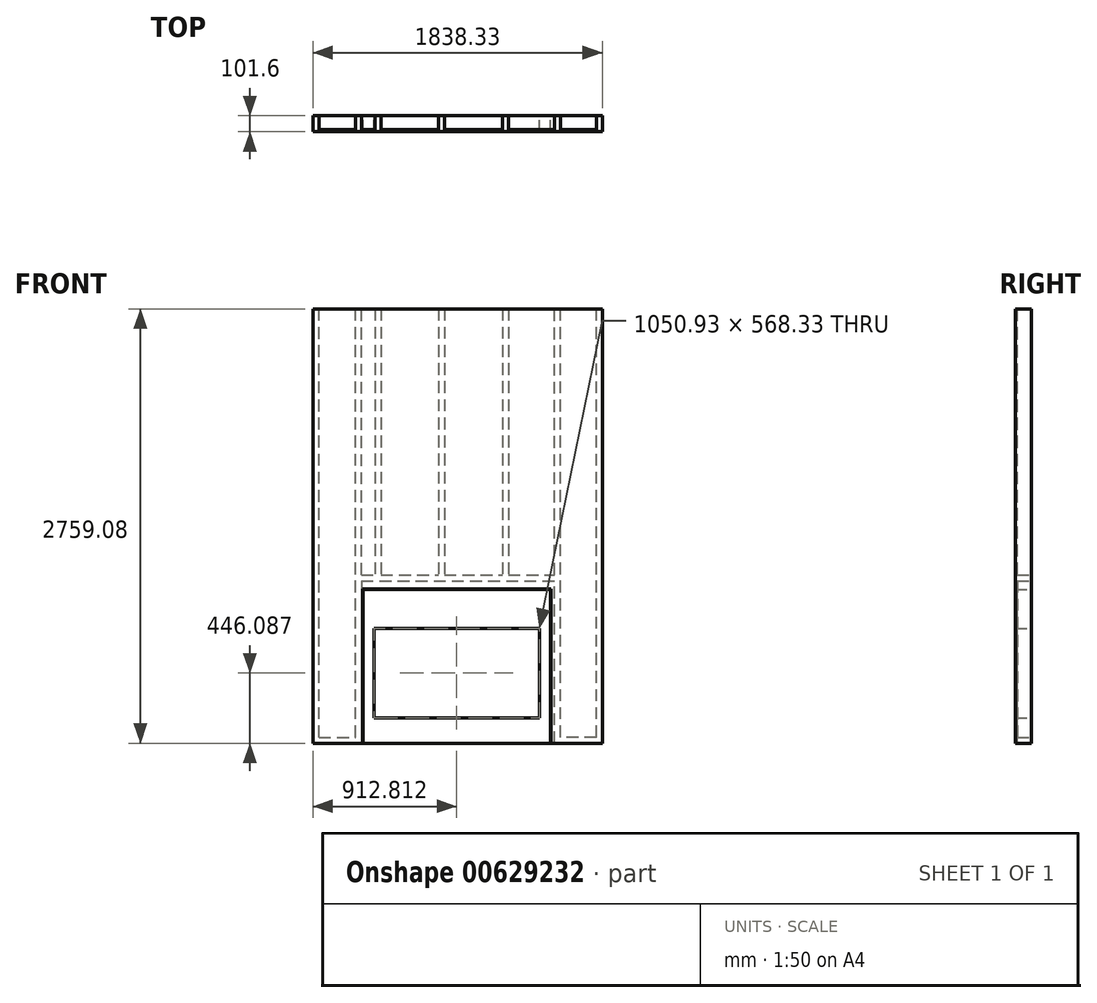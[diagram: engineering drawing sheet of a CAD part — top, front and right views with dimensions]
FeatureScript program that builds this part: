
annotation { "Feature Type Name" : "Feature", "Feature Type Description" : "" }
export const myFeature = defineFeature(function(context is Context, id is Id, definition is map)
    precondition{}
    {
        {
            var Q0;
            Q0=qCreatedBy(makeId("Front.planeOp"),FACE);
            var sketch = newSketch(context, id + "F0", { "sketchPlane" : qUnion([Q0])});
            skLineSegment(sketch, "E0.bottom", {"start": v(0, 38.1) * mm, "end": v(38.1, 38.1) * mm});
            skLineSegment(sketch, "E0.top", {"start": v(0, 2759.08) * mm, "end": v(38.1, 2759.08) * mm});
            skLineSegment(sketch, "E0.left", {"start": v(0, 38.1) * mm, "end": v(0, 2759.08) * mm});
            skLineSegment(sketch, "E0.right", {"start": v(38.1, 38.1) * mm, "end": v(38.1, 2759.08) * mm});
            skLineSegment(sketch, "E1.bottom", {"start": v(269.88, 38.1) * mm, "end": v(307.98, 38.1) * mm});
            skLineSegment(sketch, "E1.top", {"start": v(269.88, 2759.08) * mm, "end": v(307.98, 2759.08) * mm});
            skLineSegment(sketch, "E1.left", {"start": v(269.88, 38.1) * mm, "end": v(269.88, 2759.08) * mm});
            skLineSegment(sketch, "E1.right", {"start": v(307.98, 38.1) * mm, "end": v(307.98, 1031.88) * mm});
            skLineSegment(sketch, "E2.bottom", {"start": v(1533.53, 38.1) * mm, "end": v(1571.63, 38.1) * mm});
            skLineSegment(sketch, "E2.top", {"start": v(1533.52, 2759.08) * mm, "end": v(1571.63, 2759.08) * mm});
            skLineSegment(sketch, "E2.left", {"start": v(1533.53, 38.1) * mm, "end": v(1533.53, 1031.88) * mm});
            skLineSegment(sketch, "E2.right", {"start": v(1571.63, 38.1) * mm, "end": v(1571.63, 2759.08) * mm});
            skLineSegment(sketch, "E3.bottom", {"start": v(1800.23, 38.1) * mm, "end": v(1838.33, 38.1) * mm});
            skLineSegment(sketch, "E3.top", {"start": v(1800.23, 2759.08) * mm, "end": v(1838.33, 2759.08) * mm});
            skLineSegment(sketch, "E3.left", {"start": v(1800.23, 38.1) * mm, "end": v(1800.23, 2759.08) * mm});
            skLineSegment(sketch, "E3.right", {"start": v(1838.33, 38.1) * mm, "end": v(1838.33, 2759.08) * mm});
            skLineSegment(sketch, "E4", {"start": v(1838.33, 38.1) * mm, "end": v(1838.33, 0) * mm});
            skLineSegment(sketch, "E5", {"start": v(1838.33, 0) * mm, "end": v(1533.53, 0) * mm});
            skLineSegment(sketch, "E6", {"start": v(0, 0) * mm, "end": v(0, 38.1) * mm});
            skLineSegment(sketch, "E7", {"start": v(38.1, 38.1) * mm, "end": v(269.88, 38.1) * mm});
            skLineSegment(sketch, "E8", {"start": v(1800.23, 38.1) * mm, "end": v(1571.63, 38.1) * mm});
            skLineSegment(sketch, "E9", {"start": v(38.1, 2759.08) * mm, "end": v(269.88, 2759.08) * mm, "construction": true});
            skLineSegment(sketch, "E10", {"start": v(1571.63, 2759.08) * mm, "end": v(1800.23, 2759.08) * mm, "construction": true});
            skLineSegment(sketch, "E11", {"start": v(307.98, 1031.88) * mm, "end": v(1533.53, 1031.88) * mm});
            skLineSegment(sketch, "E12", {"start": v(307.98, 1069.98) * mm, "end": v(1533.53, 1069.98) * mm});
            skLineSegment(sketch, "E13.trimOffspring", {"start": v(307.98, 1069.98) * mm, "end": v(307.98, 2759.08) * mm});
            skLineSegment(sketch, "E14.trimOffspring", {"start": v(1533.53, 1069.98) * mm, "end": v(1533.52, 2759.08) * mm});
            skLineSegment(sketch, "E15", {"start": v(1533.53, 1031.88) * mm, "end": v(1533.53, 1069.98) * mm});
            skLineSegment(sketch, "E16", {"start": v(307.98, 1031.88) * mm, "end": v(307.98, 1069.98) * mm});
            skLineSegment(sketch, "E17", {"start": v(393.7, 2759.08) * mm, "end": v(393.7, 1069.98) * mm});
            skLineSegment(sketch, "E18", {"start": v(431.8, 2759.08) * mm, "end": v(431.8, 1069.98) * mm});
            skLineSegment(sketch, "E19", {"start": v(835.02, 2759.08) * mm, "end": v(835.02, 1069.98) * mm});
            skLineSegment(sketch, "E20", {"start": v(1203.32, 2759.08) * mm, "end": v(1241.42, 2759.08) * mm});
            skLineSegment(sketch, "E21", {"start": v(1241.42, 2759.08) * mm, "end": v(1241.42, 1069.98) * mm});
            skLineSegment(sketch, "E22", {"start": v(1203.32, 2759.08) * mm, "end": v(1203.33, 1069.98) * mm});
            skLineSegment(sketch, "E23", {"start": v(835.02, 2759.08) * mm, "end": v(796.92, 2759.08) * mm});
            skLineSegment(sketch, "E24", {"start": v(796.92, 2759.08) * mm, "end": v(796.92, 1069.98) * mm});
            skLineSegment(sketch, "E25", {"start": v(393.7, 2759.08) * mm, "end": v(431.8, 2759.08) * mm});
            skLineSegment(sketch, "E26", {"start": v(307.98, 2759.08) * mm, "end": v(393.7, 2759.08) * mm, "construction": true});
            skLineSegment(sketch, "E27", {"start": v(796.92, 2759.08) * mm, "end": v(431.8, 2759.08) * mm, "construction": true});
            skLineSegment(sketch, "E28", {"start": v(1203.32, 2759.08) * mm, "end": v(835.02, 2759.08) * mm, "construction": true});
            skLineSegment(sketch, "E29", {"start": v(1533.52, 2759.08) * mm, "end": v(1241.42, 2759.08) * mm, "construction": true});
            skLineSegment(sketch, "E30", {"start": v(307.98, 38.1) * mm, "end": v(307.98, 0) * mm});
            skLineSegment(sketch, "E31", {"start": v(1533.53, 38.1) * mm, "end": v(1533.53, 0) * mm});
            skLineSegment(sketch, "E32.trimOffspring", {"start": v(307.98, 0) * mm, "end": v(0, 0) * mm});
            skLineSegment(sketch, "E33", {"start": v(307.98, 0) * mm, "end": v(1533.53, 0) * mm, "construction": true});
            skLineSegment(sketch, "E34", {"start": v(307.97, 38.1) * mm, "end": v(1533.53, 38.1) * mm, "construction": true});
            skSolve(sketch);
        }
        {
            var Q0;
            Q0 = qSketchRegion(id + "F0", true);
            extrude(context, id + "F1", {"entities" : qUnion([Q0]), "depth" : 88.9 * mm, "offsetDistance" : 25.4 * mm});
        }
        {
            var Q0;
            Q0=makeQuery(id+"F1.opExtrude","CAP_FACE",FACE,{"disambiguationData":[OSD([sQuery(id+"F0.wireOp",EDGE,"E0.top"),sQuery(id+"F0.wireOp",EDGE,"E0.left"),sQuery(id+"F0.wireOp",EDGE,"E0.right"),sQuery(id+"F0.wireOp",EDGE,"E1.top"),sQuery(id+"F0.wireOp",EDGE,"E1.left"),sQuery(id+"F0.wireOp",EDGE,"E1.right"),sQuery(id+"F0.wireOp",EDGE,"E2.top"),sQuery(id+"F0.wireOp",EDGE,"E2.left"),sQuery(id+"F0.wireOp",EDGE,"E2.right"),sQuery(id+"F0.wireOp",EDGE,"E3.top"),sQuery(id+"F0.wireOp",EDGE,"E3.left"),sQuery(id+"F0.wireOp",EDGE,"E3.right"),sQuery(id+"F0.wireOp",EDGE,"E4"),sQuery(id+"F0.wireOp",EDGE,"E5"),sQuery(id+"F0.wireOp",EDGE,"E6"),sQuery(id+"F0.wireOp",EDGE,"E7"),sQuery(id+"F0.wireOp",EDGE,"KnR4iRTG-fG3G-GNrI-prFG-BcDMh5IJVTdv"),sQuery(id+"F0.wireOp",EDGE,"E8"),sQuery(id+"F0.wireOp",EDGE,"E11"),sQuery(id+"F0.wireOp",EDGE,"E12"),sQuery(id+"F0.wireOp",EDGE,"E13.trimOffspring"),sQuery(id+"F0.wireOp",EDGE,"E14.trimOffspring"),sQuery(id+"F0.wireOp",EDGE,"E17"),sQuery(id+"F0.wireOp",EDGE,"E18"),sQuery(id+"F0.wireOp",EDGE,"E19"),sQuery(id+"F0.wireOp",EDGE,"E20"),sQuery(id+"F0.wireOp",EDGE,"E21"),sQuery(id+"F0.wireOp",EDGE,"E22"),sQuery(id+"F0.wireOp",EDGE,"E23"),sQuery(id+"F0.wireOp",EDGE,"E24"),sQuery(id+"F0.wireOp",EDGE,"E25")])],"isStart":true});
            var sketch = newSketch(context, id + "F2", { "sketchPlane" : qUnion([Q0])});
            skLineSegment(sketch, "E35.bottom", {"start": v(-317.5, 977.9) * mm, "end": v(-1508.13, 977.9) * mm});
            skLineSegment(sketch, "E35.top", {"start": v(-317.5, 0) * mm, "end": v(-1508.13, 0) * mm});
            skLineSegment(sketch, "E35.left", {"start": v(-317.5, 977.9) * mm, "end": v(-317.5, 0) * mm});
            skLineSegment(sketch, "E35.right", {"start": v(-1508.13, 977.9) * mm, "end": v(-1508.13, 0) * mm});
            skLineSegment(sketch, "E36.bottom", {"start": v(-387.35, 730.25) * mm, "end": v(-1438.28, 730.25) * mm});
            skLineSegment(sketch, "E36.top", {"start": v(-387.35, 161.93) * mm, "end": v(-1438.28, 161.93) * mm});
            skLineSegment(sketch, "E36.left", {"start": v(-387.35, 730.25) * mm, "end": v(-387.35, 161.93) * mm});
            skLineSegment(sketch, "E36.right", {"start": v(-1438.28, 730.25) * mm, "end": v(-1438.28, 161.93) * mm});
            skSolve(sketch);
        }
        {
            var Q0;
            Q0 = qSketchRegion(id + "F2", true);
            extrude(context, id + "F3", {"entities" : qUnion([Q0]), "operationType" : NewBodyOperationType.ADD, "oppositeDirection" : true, "depth" : 101.6 * mm, "offsetDistance" : 25.4 * mm});
        }
        {
            var Q0;
            Q0=makeQuery(id+"F1.opExtrude","CAP_FACE",FACE,{"disambiguationData":[OSD([sQuery(id+"F0.wireOp",EDGE,"E0.top"),sQuery(id+"F0.wireOp",EDGE,"E0.left"),sQuery(id+"F0.wireOp",EDGE,"E0.right"),sQuery(id+"F0.wireOp",EDGE,"E1.top"),sQuery(id+"F0.wireOp",EDGE,"E1.left"),sQuery(id+"F0.wireOp",EDGE,"E1.right"),sQuery(id+"F0.wireOp",EDGE,"E2.top"),sQuery(id+"F0.wireOp",EDGE,"E2.left"),sQuery(id+"F0.wireOp",EDGE,"E2.right"),sQuery(id+"F0.wireOp",EDGE,"E3.top"),sQuery(id+"F0.wireOp",EDGE,"E3.left"),sQuery(id+"F0.wireOp",EDGE,"E3.right"),sQuery(id+"F0.wireOp",EDGE,"E4"),sQuery(id+"F0.wireOp",EDGE,"E5"),sQuery(id+"F0.wireOp",EDGE,"E6"),sQuery(id+"F0.wireOp",EDGE,"E7"),sQuery(id+"F0.wireOp",EDGE,"E8"),sQuery(id+"F0.wireOp",EDGE,"E11"),sQuery(id+"F0.wireOp",EDGE,"E12"),sQuery(id+"F0.wireOp",EDGE,"E13.trimOffspring"),sQuery(id+"F0.wireOp",EDGE,"E14.trimOffspring"),sQuery(id+"F0.wireOp",EDGE,"E17"),sQuery(id+"F0.wireOp",EDGE,"E18"),sQuery(id+"F0.wireOp",EDGE,"E19"),sQuery(id+"F0.wireOp",EDGE,"E20"),sQuery(id+"F0.wireOp",EDGE,"E21"),sQuery(id+"F0.wireOp",EDGE,"E22"),sQuery(id+"F0.wireOp",EDGE,"E23"),sQuery(id+"F0.wireOp",EDGE,"E24"),sQuery(id+"F0.wireOp",EDGE,"E25"),sQuery(id+"F0.wireOp",EDGE,"E30"),sQuery(id+"F0.wireOp",EDGE,"E31"),sQuery(id+"F0.wireOp",EDGE,"E32.trimOffspring")])],"isStart":false});
            var sketch = newSketch(context, id + "F4", { "sketchPlane" : qUnion([Q0])});
            skLineSegment(sketch, "E37.bottom", {"start": v(0, 2759.08) * mm, "end": v(1838.33, 2759.08) * mm});
            skLineSegment(sketch, "E37.top", {"start": v(0, 981.08) * mm, "end": v(1838.33, 981.08) * mm});
            skLineSegment(sketch, "E37.left", {"start": v(0, 2759.08) * mm, "end": v(0, 981.08) * mm});
            skLineSegment(sketch, "E37.right", {"start": v(1838.33, 2759.08) * mm, "end": v(1838.33, 981.08) * mm});
            skLineSegment(sketch, "E38", {"start": v(0, 981.08) * mm, "end": v(0, 0) * mm});
            skLineSegment(sketch, "E39", {"start": v(0, 0) * mm, "end": v(314.33, 0) * mm});
            skLineSegment(sketch, "E40", {"start": v(314.33, 0) * mm, "end": v(314.33, 981.08) * mm});
            skLineSegment(sketch, "E41", {"start": v(1511.3, 0) * mm, "end": v(1838.33, 0) * mm});
            skLineSegment(sketch, "E42", {"start": v(1511.3, 0) * mm, "end": v(1511.3, 981.08) * mm});
            skLineSegment(sketch, "E43", {"start": v(1838.33, 0) * mm, "end": v(1838.33, 981.08) * mm});
            skLineSegment(sketch, "E44", {"start": v(412.75, 2759.07) * mm, "end": v(412.75, 981.08) * mm});
            skLineSegment(sketch, "E45", {"start": v(1838.33, 1844.67) * mm, "end": v(412.75, 1844.67) * mm});
            skLineSegment(sketch, "E46.bottom", {"start": v(2555.78, 2713.26) * mm, "end": v(4079.78, 2713.26) * mm, "construction": true});
            skLineSegment(sketch, "E46.top", {"start": v(2555.78, 1798.86) * mm, "end": v(4079.78, 1798.86) * mm, "construction": true});
            skLineSegment(sketch, "E46.left", {"start": v(2555.78, 2713.26) * mm, "end": v(2555.78, 1798.86) * mm, "construction": true});
            skLineSegment(sketch, "E46.right", {"start": v(4079.78, 2713.26) * mm, "end": v(4079.78, 1798.86) * mm, "construction": true});
            skLineSegment(sketch, "E47", {"start": v(3981.36, 2713.26) * mm, "end": v(3981.36, 1798.86) * mm, "construction": true});
            skLineSegment(sketch, "E48.bottom", {"start": v(2538.54, 1648.21) * mm, "end": v(4062.54, 1648.21) * mm, "construction": true});
            skLineSegment(sketch, "E48.top", {"start": v(2538.54, 733.81) * mm, "end": v(4062.54, 733.81) * mm, "construction": true});
            skLineSegment(sketch, "E48.left", {"start": v(2538.54, 1648.21) * mm, "end": v(2538.54, 733.81) * mm, "construction": true});
            skLineSegment(sketch, "E48.right", {"start": v(4062.54, 1648.21) * mm, "end": v(4062.54, 733.81) * mm, "construction": true});
            skLineSegment(sketch, "E49.bottom", {"start": v(4398.77, 2716) * mm, "end": v(5922.77, 2716) * mm, "construction": true});
            skLineSegment(sketch, "E49.top", {"start": v(4398.77, 1801.6) * mm, "end": v(5922.77, 1801.6) * mm, "construction": true});
            skLineSegment(sketch, "E49.left", {"start": v(4398.77, 2716) * mm, "end": v(4398.77, 1801.6) * mm, "construction": true});
            skLineSegment(sketch, "E49.right", {"start": v(5922.77, 2716) * mm, "end": v(5922.77, 1801.6) * mm, "construction": true});
            skLineSegment(sketch, "E50", {"start": v(3964.11, 1648.21) * mm, "end": v(3964.11, 733.81) * mm, "construction": true});
            skLineSegment(sketch, "E51", {"start": v(2538.54, 784.61) * mm, "end": v(3964.11, 784.61) * mm, "construction": true});
            skLineSegment(sketch, "E52", {"start": v(5379.85, 2716) * mm, "end": v(5379.85, 1801.6) * mm, "construction": true});
            skLineSegment(sketch, "E53", {"start": v(5379.85, 2388.97) * mm, "end": v(4398.77, 2388.97) * mm, "construction": true});
            skLineSegment(sketch, "E54", {"start": v(5379.85, 2074.64) * mm, "end": v(4398.77, 2074.64) * mm, "construction": true});
            skLineSegment(sketch, "E55", {"start": v(412.75, 1844.67) * mm, "end": v(0, 1844.67) * mm});
            skLineSegment(sketch, "E56", {"start": v(5510.02, 2716) * mm, "end": v(5510.02, 1801.6) * mm, "construction": true});
            skLineSegment(sketch, "E57.bottom", {"start": v(4462.38, 1641.77) * mm, "end": v(5928.15, 1641.77) * mm, "construction": true});
            skLineSegment(sketch, "E57.top", {"start": v(4462.38, 723.02) * mm, "end": v(5928.15, 723.02) * mm, "construction": true});
            skLineSegment(sketch, "E57.left", {"start": v(4462.38, 1641.77) * mm, "end": v(4462.38, 723.02) * mm, "construction": true});
            skLineSegment(sketch, "E57.right", {"start": v(5928.15, 1641.77) * mm, "end": v(5928.15, 723.02) * mm, "construction": true});
            skLineSegment(sketch, "E58", {"start": v(5515.4, 1641.77) * mm, "end": v(5515.4, 723.02) * mm, "construction": true});
            skLineSegment(sketch, "E59", {"start": v(5515.4, 778.17) * mm, "end": v(5928.15, 778.17) * mm, "construction": true});
            skSolve(sketch);
        }
        {
            var Q0;
            Q0 = qSketchRegion(id + "F4", true);
            extrude(context, id + "F5", {"entities" : qUnion([Q0]), "operationType" : NewBodyOperationType.ADD, "depth" : 12.7 * mm, "offsetDistance" : 25.4 * mm});
        }
    });
